# Revit family: Grohe_PlumbingFixture_Tempesta100_HandShower_28419002a
name_source: partatom
category: Plumbing Fixtures
revit_build: Autodesk Revit 2018 (Build: 20190510_1515(x64)
units: mm (PartAtom-declared; Revit-internal decimal feet)

## family parameters
Cut with Voids When Loaded = No
Host = Face
OmniClass Number = 23.65.00.00
OmniClass Title = Supply and Distribution of Liquids and Gases
Part Type = Normal
Room Calculation Point = No
Round Connector Dimension = Use Diameter
Shared = No

## types (1)
- 28419002
    ADACompliant = No
    Assembly Code = D2010700
    BIMObjectName = Grohe_PlumbingFixture_Tempesta100_HandShower_28419002
    ClassificationName = Uniclass 2015
    ClassificationValue = Pr_40_20_87_76
    ColdWaterConnectionDiameter = 10 mm  [stored 0.0328084 ft]
    Color = Chrome
    Default Elevation = 0 mm  [stored 0 ft]
    Description = With its flowing modern curves and trusty performance the Tempesta hand shower 100 is a quick way to make the daily shower even more enjoyable. All you have to do is screw it onto a standard hose! Built using precision German engineering, it feels comfortable in the hand and looks perfect in a wide range of bathroom designs. It also delivers a choice of three GROHE sprays: Rain spray, which is as soothing as soft summer rain, the lighter than air Rain O² spray and the pulsating and revitalising Massage Spray. It is also packed with GROHE technology. GROHE DreamSpray ensures the flow of water from every nozzle is balanced and even whichever spray type you choose. GROHE EcoJoy limits the water flow to 9.5 l/min but still delivers pure and satisfying indulgence. The dazzling scratch resistant GROHE StarLight chrome keeps its sparkle for a lifetime and you can clear the SpeedClean nozzles of limescale with a simple wipe. The ShockProof silicone ring prevents damage if the handshower is dropped and the Inner WaterGuide prevents the surface of the shower from getting hot, protecting both your skin and the chrome finish. The GROHE Tempesta range – a beautifully crafted blend of modern style and performance!
    DocumentationCertificates = https://www.bimstore.co
    DocumentationInstallationGuide = https://www.bimstore.co
    DocumentationLiterature = https://www.bimstore.co
    DocumentationMaintenance = https://www.bimstore.co
    DocumentationTechnical = https://www.bimstore.co
    DurationUnit = Years
    Ecojoy = No
    ExpectedLife = 0
    Features = With its flowing modern curves and trusty performance the Tempesta hand shower 100 is a quick way to make the daily shower even more enjoyable. All you have to do is screw it onto a standard hose! Built using precision German engineering, it feels comfortable in the hand and looks perfect in a wide range of bathroom designs. It also delivers a choice of three GROHE sprays: Rain spray, which is as soothing as soft summer rain, the lighter than air Rain O² spray and the pulsating and revitalising Massage Spray. It is also packed with GROHE technology. GROHE DreamSpray ensures the flow of water from every nozzle is balanced and even whichever spray type you choose. GROHE EcoJoy limits the water flow to 9.5 l/min but still delivers pure and satisfying indulgence. The dazzling scratch resistant GROHE StarLight chrome keeps its sparkle for a lifetime and you can clear the SpeedClean nozzles of limescale with a simple wipe. The ShockProof silicone ring prevents damage if the handshower is dropped and the Inner WaterGuide prevents the surface of the shower from getting hot, protecting both your skin and the chrome finish. The GROHE Tempesta range – a beautifully crafted blend of modern style and performance!
    HotWaterConnectionDiameter = 10 mm  [stored 0.0328084 ft]
    IfcExportAs = IfcPipeFitting
    IfcExportType = IfcPipeFittingType
    Keynote = N13
    LowEmittingMaterial = No
    Manufacturer = Grohe
    ManufacturerName = Grohe
    MasterformatNumber = 01 52 19
    MasterformatTitle = Sanitary Facilities
    Model = Tempesta 100 - Hand shower 3 sprays
    ModelNumber = 28419002
    ModelReference = Tempesta 100 - Hand shower 3 sprays
    NBSDescription = Shower heads
    NBSObjectName = Grohe - Shower heads
    NBSReference = 45-35-70/333
    NominalDepth = 0 mm  [stored 0 ft]
    NominalHeight = 0 mm  [stored 0 ft]
    NominalLength = 0 mm  [stored 0 ft]
    PrimaryMaterial = Steel, Chrome Plated
    ProductDocumentationLink = https://www.grohe.co.uk
    ProductPageURL = https://www.grohe.co.uk
    ProductionYear = 2020
    Type Comments = 28419002
    TypeName = Tempesta 100 - Hand shower 3 sprays
    URL = https://www.grohe.co.uk
    WarrantyDurationLabor = 0
    WarrantyDurationParts = 0
    WarrantyDurationUnit = Years
    _BSBibleVersion = 16
    _BimSpecGuid = 0
    _CurrentRevision = 1
    _DistributedBy = www.bimstore.co
    _ObjectUserGuide = https://www.bimstore.co

note: [stored X ft] marks values corroborated as IEEE doubles in the binary element streams (Revit-internal decimal feet)

## geometry (parser evidence)
native form markers: Sweep x2
no freeform markers — native parametric forms only
